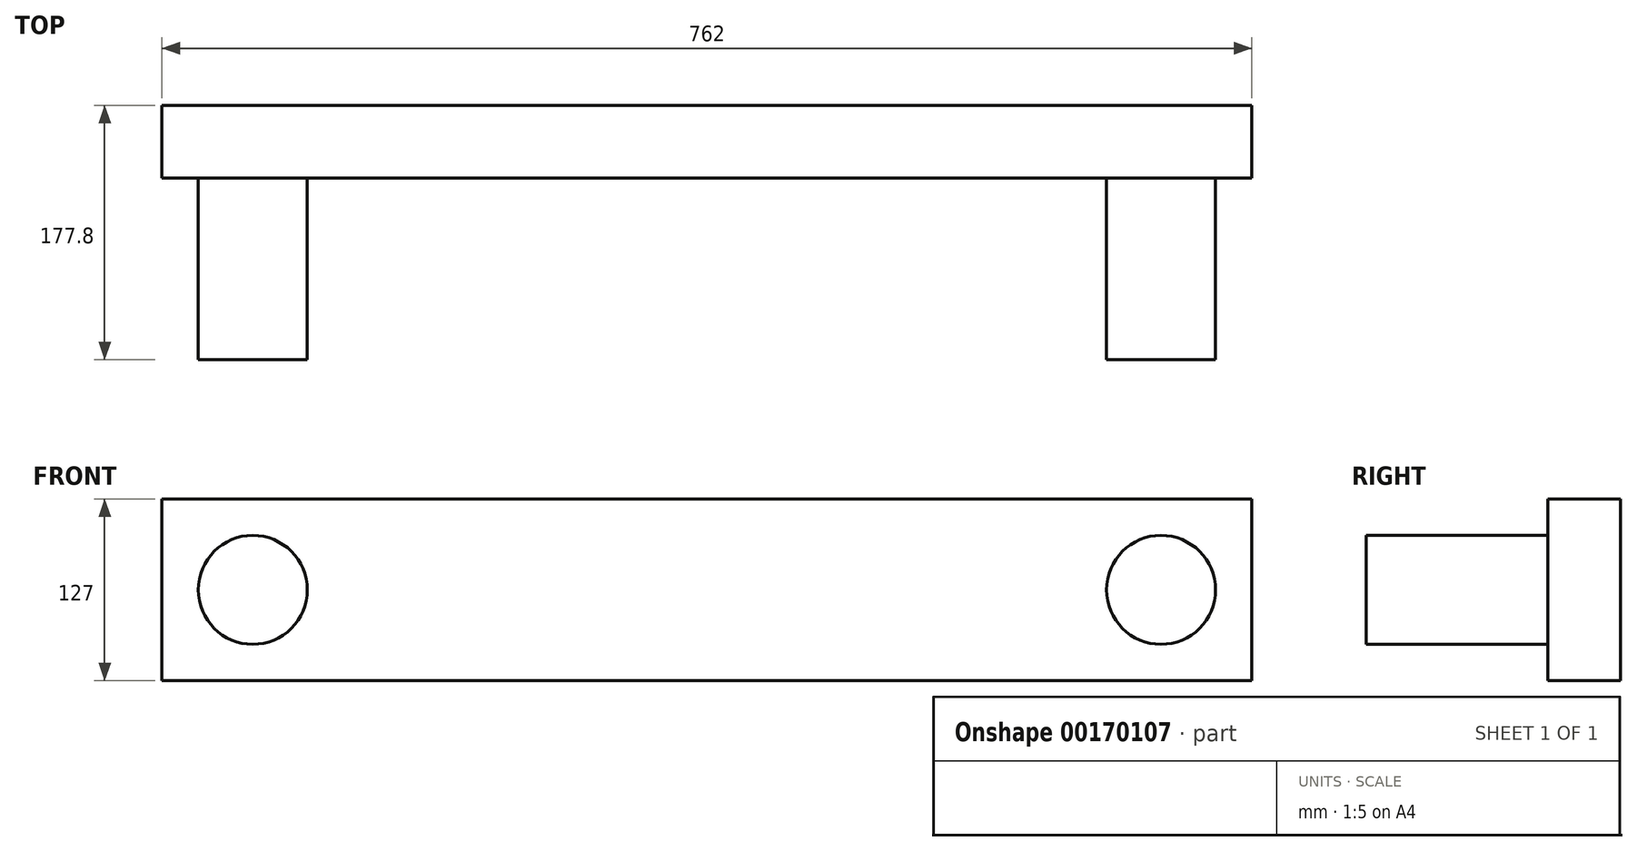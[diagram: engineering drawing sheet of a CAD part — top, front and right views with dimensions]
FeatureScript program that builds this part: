
annotation { "Feature Type Name" : "Feature", "Feature Type Description" : "" }
export const myFeature = defineFeature(function(context is Context, id is Id, definition is map)
    precondition{}
    {
        {
            var Q0;
            Q0=qCreatedBy(makeId("Front.planeOp"),FACE);
            var sketch = newSketch(context, id + "F0", { "sketchPlane" : qUnion([Q0])});
            skLineSegment(sketch, "E0.bottom", {"start": v(-391, 0) * mm, "end": v(371, 0) * mm});
            skLineSegment(sketch, "E0.top", {"start": v(-391, 127) * mm, "end": v(371, 127) * mm});
            skLineSegment(sketch, "E0.left", {"start": v(-391, 0) * mm, "end": v(-391, 127) * mm});
            skLineSegment(sketch, "E0.right", {"start": v(371, 0) * mm, "end": v(371, 127) * mm});
            skSolve(sketch);
        }
        {
            var Q0;
            Q0=makeQuery(id+"F0.imprint","IMPRINT",FACE,{"disambiguationData":[TD([[makeQuery(id+"F0.imprint","IMPRINT",EDGE,{"derivedFrom":sQuery(id+"F0.wireOp",EDGE,"E0.bottom")}),1.0]])]});
            extrude(context, id + "F1", {"entities" : qUnion([Q0]), "depth" : 50.8 * mm});
        }
        {
            var Q0;
            Q0=makeQuery(id+"F1.opExtrude","CAP_FACE",FACE,{"disambiguationData":[OSD([sQuery(id+"F0.wireOp",EDGE,"E0.bottom"),sQuery(id+"F0.wireOp",EDGE,"E0.top"),sQuery(id+"F0.wireOp",EDGE,"E0.left"),sQuery(id+"F0.wireOp",EDGE,"E0.right")])],"isStart":false});
            var sketch = newSketch(context, id + "F2", { "sketchPlane" : qUnion([Q0])});
            skCircle(sketch, "E1", {"center": v(-327.5, 63.5) * mm, "radius": 38.1 * mm});
            skCircle(sketch, "E2", {"center": v(307.5, 63.5) * mm, "radius": 38.1 * mm});
            skSolve(sketch);
        }
        {
            var Q0;
            Q0=makeQuery(id+"F2.imprint","IMPRINT",FACE,{"disambiguationData":[TD([[makeQuery(id+"F2.imprint","IMPRINT",EDGE,{"derivedFrom":sQuery(id+"F2.wireOp",EDGE,"E1")}),1.0]])]});
            var Q1;
            Q1=makeQuery(id+"F2.imprint","IMPRINT",FACE,{"disambiguationData":[TD([[makeQuery(id+"F2.imprint","IMPRINT",EDGE,{"derivedFrom":sQuery(id+"F2.wireOp",EDGE,"E2")}),1.0]])]});
            extrude(context, id + "F3", {"entities" : qUnion([Q0, Q1]), "operationType" : NewBodyOperationType.ADD, "depth" : 127 * mm});
        }
    });
